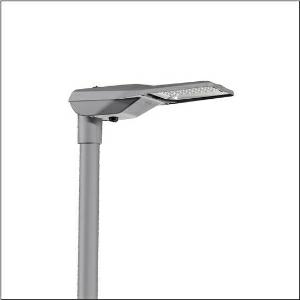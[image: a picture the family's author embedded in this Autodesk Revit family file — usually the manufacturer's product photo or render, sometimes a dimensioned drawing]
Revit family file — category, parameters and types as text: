
# Revit family: streetlight_sl_21_mini___p1_0a_5xe2a33t08hb_97bb
name_source: partatom
category: Lighting Fixtures
units: mm (PartAtom-declared; Revit-internal decimal feet)

## family parameters
Cut with Voids When Loaded = No
Host = Face
Light Source = No
Part Type = Normal
Room Calculation Point = No
Round Connector Dimension = Use Diameter
Shared = No

## types (1)
- --- (1 x LED, 9040 lm, 66 W, 3000K)
    Apparent Load = 66 VA
    CIE Flux Codes = 21 50 90 100 100
    Color Rendering = 70
    Color Temperature = 3000K
    Default Elevation = 1800 mm
    Description = Streetlight SL 21 mini, mast luminaire, primary light control with lens, of PMMA, primary optical cover: cover, of toughened safety glass, transparent, light distribution: P1.0a, light emission: direct distribution, primary light characteristic: asymmetric, installation type: side-entry, post-top, LED, High Power LED, rated luminous flux: 9.040lm, luminous efficacy: 137lm/W, light colour: 730, colour temperature: 3000K, control gear: D4i, control: overheat protection, constant luminous flux control, time-dependent luminous flux control, flexible luminous flux parameterisation, pre-setting: logarithmic dimming characteristic, mains connection: 220..240V, AC, 50/60Hz, start of lifetime: 66W, end of service life: 69W, reduction: 30W, luminaire housing, of diecast aluminium, powder-coated, Siteco® metallic grey (DB 702S), corrosivity category C5 mid according to DIN EN ISO 12944, please order mast flange separately, inclination adjustable: 0°, 5°, 10°, 15°, sealing non-destructively replaceable, multi-level sealing system, length: 628mm, width: 235mm, height: 110mm, mast flange for spigot size: 42mm (side-entry): 5XC10008XM4, 60/48mm (side-entry/post-top): 5XC10108XM2, 76/60mm (side-entry/post-top): 5XC10108XM1, mounting height: 4..8m, Smart Interface below and above, protection rating (complete): IP66, insulation class (complete): insulation class II (safety insulation), certification: CE, ENEC, ENEC+, VDE, impact resistance: IK10, permissible operating ambient temperature for outdoor applications: -40..+50°C, standard-compliant lighting for roads and squares, packaging unit: 1 piece

Light Distribution: P1.0a
    Height = 110 mm
    Lamp = 1 x LED
    Lamp Light Flux = 9040 lm
    Lamp Power = 66 W
    Lamp count = 1
    Length = 625 mm
    Luminous efficacy = 137 lm/W
    Manufacturer = Siteco
    ModVariant = No
    Model = 5XE2A33T08HB
    Number of Poles = 1
    OnlyDefault = Yes
    Power Factor = 1
    Product Name = Streetlight SL 21 mini | P1.0a
    Product group = mast luminaire | pylon top
    ProductGroupID = 6100
    Protection Class = Protection class II
    Protection Degree = IP 66
    RLX_Detail_Level = 1
    RLX_Emergency_Light_Flux = 0 lm
    RLX_Emergency_Type = 0
    RLX_Emergency_Type_DB = No
    RlxData = <blob elided: 37629 chars, md5=a650faa6>
    Socket = socket
    Standby Power = 0 W
    System Light Flux = 9040 lm
    System Power = 66 W
    Type Comments = factory setting: luminous flux: 100 % | dim-lin: 254 | 670 mA
    Type Image = l_1003514.jpg
    URL = http://relux.com
    VarID = @adj_207779
    Voltage = 0 V
    Weight = 0.00 kg
    Width = 234 mm

## geometry (parser evidence)
native form markers: Blend x4, Sweep x9
no freeform markers — native parametric forms only
